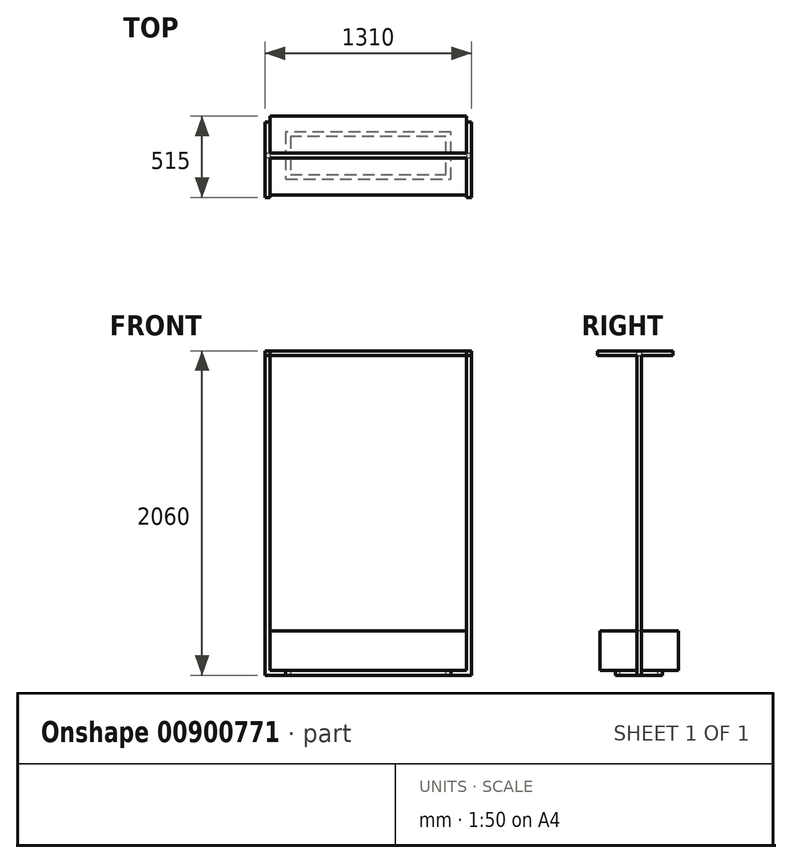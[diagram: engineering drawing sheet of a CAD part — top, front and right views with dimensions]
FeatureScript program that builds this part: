
annotation { "Feature Type Name" : "Feature", "Feature Type Description" : "" }
export const myFeature = defineFeature(function(context is Context, id is Id, definition is map)
    precondition{}
    {
        {
            var Q0;
            Q0=qCreatedBy(makeId("Top.planeOp"),FACE);
            var sketch = newSketch(context, id + "F0", { "sketchPlane" : qUnion([Q0])});
            skLineSegment(sketch, "E0.bottom", {"start": v(-625, 250) * mm, "end": v(625, 250) * mm});
            skLineSegment(sketch, "E0.top", {"start": v(-625, -250) * mm, "end": v(625, -250) * mm});
            skLineSegment(sketch, "E0.left", {"start": v(-625, 250) * mm, "end": v(-625, -250) * mm});
            skLineSegment(sketch, "E0.right", {"start": v(625, 250) * mm, "end": v(625, -250) * mm});
            skLineSegment(sketch, "E1", {"start": v(-625, 250) * mm, "end": v(625, -250) * mm, "construction": true});
            skSolve(sketch);
        }
        {
            var Q0;
            Q0=qSketchRegion(id+"F0",true);
            extrude(context, id + "F1", {"entities" : qUnion([Q0]), "depth" : 250 * mm, "offsetDistance" : 25 * mm});
        }
        {
            var Q0;
            Q0=qCreatedBy(makeId("Front.planeOp"),FACE);
            var sketch = newSketch(context, id + "F2", { "sketchPlane" : qUnion([Q0])});
            skLineSegment(sketch, "E2", {"start": v(625, 0) * mm, "end": v(625, 2000) * mm});
            skLineSegment(sketch, "E3", {"start": v(625, 2000) * mm, "end": v(-625, 2000) * mm});
            skLineSegment(sketch, "E4", {"start": v(-625, 2000) * mm, "end": v(-625, 0) * mm});
            skLineSegment(sketch, "E5", {"start": v(-625, 0) * mm, "end": v(625, 0) * mm});
            skLineSegment(sketch, "E6.0", {"start": v(655, 2030) * mm, "end": v(-655, 2030) * mm});
            skLineSegment(sketch, "E6.1", {"start": v(655, -30) * mm, "end": v(655, 2030) * mm});
            skLineSegment(sketch, "E6.2", {"start": v(-655, -30) * mm, "end": v(655, -30) * mm});
            skLineSegment(sketch, "E6.3", {"start": v(-655, 2030) * mm, "end": v(-655, -30) * mm});
            skSolve(sketch);
        }
        {
            var Q0;
            Q0=qSketchRegion(id+"F2",true);
            extrude(context, id + "F3", {"entities" : qUnion([Q0]), "endBound" : BoundingType.SYMMETRIC, "depth" : 30 * mm, "offsetDistance" : 25 * mm});
        }
        {
            var Q0;
            Q0=makeQuery(id+"F1.opExtrude","CAP_FACE",FACE,{"disambiguationData":[OSD([sQuery(id+"F0.wireOp",EDGE,"E0.bottom"),sQuery(id+"F0.wireOp",EDGE,"E0.top"),sQuery(id+"F0.wireOp",EDGE,"E0.left"),sQuery(id+"F0.wireOp",EDGE,"E0.right")])],"isStart":true});
            var sketch = newSketch(context, id + "F4", { "sketchPlane" : qUnion([Q0])});
            skLineSegment(sketch, "E7", {"start": v(525, 150) * mm, "end": v(525, -150) * mm});
            skLineSegment(sketch, "E8", {"start": v(525, -150) * mm, "end": v(-525, -150) * mm});
            skLineSegment(sketch, "E9", {"start": v(-525, -150) * mm, "end": v(-525, 150) * mm});
            skLineSegment(sketch, "E10", {"start": v(-525, 150) * mm, "end": v(525, 150) * mm});
            skLineSegment(sketch, "E11.0", {"start": v(-495, 120) * mm, "end": v(495, 120) * mm});
            skLineSegment(sketch, "E11.1", {"start": v(-495, -120) * mm, "end": v(-495, 120) * mm});
            skLineSegment(sketch, "E11.2", {"start": v(495, -120) * mm, "end": v(-495, -120) * mm});
            skLineSegment(sketch, "E11.3", {"start": v(495, 120) * mm, "end": v(495, -120) * mm});
            skSolve(sketch);
        }
        {
            var Q0;
            Q0=qSketchRegion(id+"F4",true);
            extrude(context, id + "F5", {"entities" : qUnion([Q0]), "operationType" : NewBodyOperationType.ADD, "depth" : 30 * mm, "offsetDistance" : 25 * mm});
        }
        {
            var Q0;
            {var subQ8=sQuery(id+"F2.wireOp",EDGE,"E5");var subQ9=sQuery(id+"F2.wireOp",EDGE,"E4");var subQ10=sQuery(id+"F2.wireOp",EDGE,"E6.3");var subQ11=sQuery(id+"F2.wireOp",EDGE,"E6.2");var subQ12=sQuery(id+"F2.wireOp",EDGE,"E6.1");var subQ13=sQuery(id+"F2.wireOp",EDGE,"E6.0");var subQ14=sQuery(id+"F2.wireOp",EDGE,"E2");var subQ15=sQuery(id+"F2.wireOp",EDGE,"E3");Q0=makeQuery(id+"F5.boolean.opBoolean","SPLIT",FACE,{"disambiguationData":[TD([makeQuery(id+"F3.opExtrude","SWEPT_FACE",FACE,{"disambiguationData":[OSD([subQ14])]})])],"derivedFrom":makeQuery(id+"F3.opExtrude","CAP_FACE",FACE,{"disambiguationData":[OSD([subQ14,subQ15,subQ9,subQ8,subQ13,subQ12,subQ11,subQ10])],"isStart":false})});}
            var sketch = newSketch(context, id + "F6", { "sketchPlane" : qUnion([Q0])});
            skLineSegment(sketch, "E12.bottom", {"start": v(655, 2030) * mm, "end": v(625, 2030) * mm});
            skLineSegment(sketch, "E12.top", {"start": v(655, 2000) * mm, "end": v(625, 2000) * mm});
            skLineSegment(sketch, "E12.left", {"start": v(655, 2030) * mm, "end": v(655, 2000) * mm});
            skLineSegment(sketch, "E12.right", {"start": v(625, 2030) * mm, "end": v(625, 2000) * mm});
            skLineSegment(sketch, "E13.bottom", {"start": v(-625, 2000) * mm, "end": v(-655, 2000) * mm});
            skLineSegment(sketch, "E13.top", {"start": v(-625, 2030) * mm, "end": v(-655, 2030) * mm});
            skLineSegment(sketch, "E13.left", {"start": v(-625, 2000) * mm, "end": v(-625, 2030) * mm});
            skLineSegment(sketch, "E13.right", {"start": v(-655, 2000) * mm, "end": v(-655, 2030) * mm});
            skSolve(sketch);
        }
        {
            var Q0;
            Q0 = qSketchRegion(id + "F6", true);
            extrude(context, id + "F7", {"entities" : qUnion([Q0]), "operationType" : NewBodyOperationType.ADD, "depth" : 250 * mm, "offsetDistance" : 25 * mm});
        }
        {
            var Q0;
            {var subQ8=sQuery(id+"F2.wireOp",EDGE,"E5");var subQ9=sQuery(id+"F2.wireOp",EDGE,"E4");var subQ10=sQuery(id+"F2.wireOp",EDGE,"E6.3");var subQ11=sQuery(id+"F2.wireOp",EDGE,"E6.2");var subQ12=sQuery(id+"F2.wireOp",EDGE,"E6.1");var subQ13=sQuery(id+"F2.wireOp",EDGE,"E6.0");var subQ14=sQuery(id+"F2.wireOp",EDGE,"E2");var subQ15=sQuery(id+"F2.wireOp",EDGE,"E3");Q0=makeQuery(id+"F5.boolean.opBoolean","SPLIT",FACE,{"disambiguationData":[TD([makeQuery(id+"F3.opExtrude","SWEPT_FACE",FACE,{"disambiguationData":[OSD([subQ14])]})])],"derivedFrom":makeQuery(id+"F3.opExtrude","CAP_FACE",FACE,{"disambiguationData":[OSD([subQ14,subQ15,subQ9,subQ8,subQ13,subQ12,subQ11,subQ10])],"isStart":true})});}
            var sketch = newSketch(context, id + "F8", { "sketchPlane" : qUnion([Q0])});
            skLineSegment(sketch, "E14.bottom", {"start": v(-625, 2000) * mm, "end": v(-655, 2000) * mm});
            skLineSegment(sketch, "E14.top", {"start": v(-625, 2030) * mm, "end": v(-655, 2030) * mm});
            skLineSegment(sketch, "E14.left", {"start": v(-625, 2000) * mm, "end": v(-625, 2030) * mm});
            skLineSegment(sketch, "E14.right", {"start": v(-655, 2000) * mm, "end": v(-655, 2030) * mm});
            skLineSegment(sketch, "E15.bottom", {"start": v(655, 2030) * mm, "end": v(625, 2030) * mm});
            skLineSegment(sketch, "E15.top", {"start": v(655, 2000) * mm, "end": v(625, 2000) * mm});
            skLineSegment(sketch, "E15.left", {"start": v(655, 2030) * mm, "end": v(655, 2000) * mm});
            skLineSegment(sketch, "E15.right", {"start": v(625, 2030) * mm, "end": v(625, 2000) * mm});
            skSolve(sketch);
        }
        {
            var Q0;
            Q0 = qSketchRegion(id + "F8", true);
            extrude(context, id + "F9", {"entities" : qUnion([Q0]), "operationType" : NewBodyOperationType.ADD, "depth" : 200 * mm, "offsetDistance" : 25 * mm});
        }
    });
